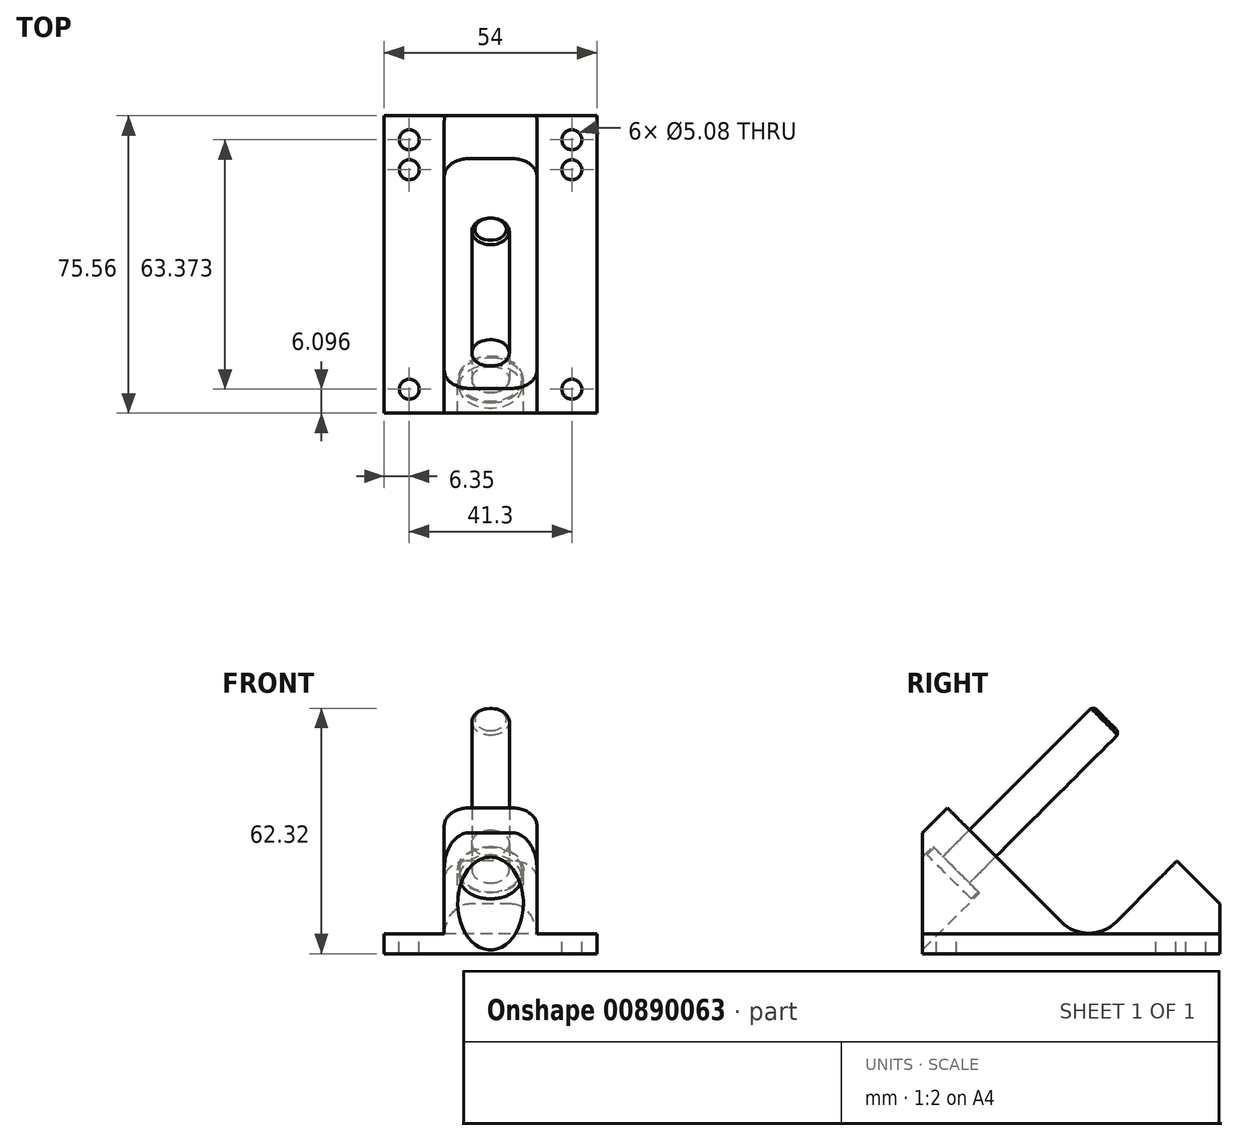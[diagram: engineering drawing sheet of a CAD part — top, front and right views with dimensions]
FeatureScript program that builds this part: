
annotation { "Feature Type Name" : "Feature", "Feature Type Description" : "" }
export const myFeature = defineFeature(function(context is Context, id is Id, definition is map)
    precondition{}
    {
        {
            var Q0;
            Q0=qCreatedBy(makeId("Right.planeOp"),FACE);
            var sketch = newSketch(context, id + "F0", { "sketchPlane" : qUnion([Q0])});
            skLineSegment(sketch, "E0", {"start": v(0, 0) * mm, "end": v(0, 30.72) * mm});
            skLineSegment(sketch, "E1", {"start": v(0, 30.72) * mm, "end": v(6.32, 37.04) * mm});
            skLineSegment(sketch, "E2", {"start": v(6.32, 37.04) * mm, "end": v(42.25, 1.12) * mm});
            skLineSegment(sketch, "E3", {"start": v(42.25, 1.12) * mm, "end": v(64.7, 23.57) * mm});
            skLineSegment(sketch, "E4", {"start": v(64.7, 23.57) * mm, "end": v(75.57, 12.7) * mm});
            skLineSegment(sketch, "E5", {"start": v(75.57, 12.7) * mm, "end": v(75.57, 0) * mm});
            skLineSegment(sketch, "E6", {"start": v(75.57, 0) * mm, "end": v(0, 0) * mm});
            skLineSegment(sketch, "E7", {"start": v(15.3, 28.06) * mm, "end": v(28.77, 41.53) * mm, "construction": true});
            skLineSegment(sketch, "E8", {"start": v(28.77, 41.53) * mm, "end": v(55.72, 14.59) * mm, "construction": true});
            skLineSegment(sketch, "E9", {"start": v(55.72, 14.59) * mm, "end": v(64.7, 5.6) * mm, "construction": true});
            skLineSegment(sketch, "E10", {"start": v(64.7, 5.6) * mm, "end": v(70.08, 11) * mm, "construction": true});
            skLineSegment(sketch, "E11", {"start": v(70.08, 11) * mm, "end": v(61.1, 19.98) * mm, "construction": true});
            skLineSegment(sketch, "E12", {"start": v(28.77, 41.53) * mm, "end": v(15.3, 55) * mm, "construction": true});
            skCircle(sketch, "E13", {"center": v(15.3, 55) * mm, "radius": 4 * mm, "construction": true});
            skLineSegment(sketch, "E14", {"start": v(64.7, 5.6) * mm, "end": v(59.3, 0.22) * mm, "construction": true});
            skLineSegment(sketch, "E15", {"start": v(59.3, 0.22) * mm, "end": v(50.33, 9.2) * mm, "construction": true});
            skCircle(sketch, "E16", {"center": v(57.51, 12.8) * mm, "radius": 5.08 * mm, "construction": true});
            skSolve(sketch);
        }
        {
            var Q0;
            Q0 = qSketchRegion(id + "F0", true);
            extrude(context, id + "F1", {"entities" : qUnion([Q0]), "depth" : 27 * mm, "offsetDistance" : 25.4 * mm});
        }
        {
            var Q0;
            Q0=makeQuery(id+"F1.opExtrude","SWEPT_EDGE",EDGE,{"disambiguationData":[OSD([sQuery(id+"F0.wireOp",EDGE,"E2"),sQuery(id+"F0.wireOp",EDGE,"E3")])]});
            fillet(context, id + "F2", {"entities" : qUnion([Q0]), "radius" : 9.9 * mm, "tangentPropagation" : true, "allowEdgeOverflow" : false});
        }
        {
            var Q0;
            Q0=makeQuery(id+"F1.opExtrude","CAP_FACE",FACE,{"disambiguationData":[OSD([sQuery(id+"F0.wireOp",EDGE,"E0"),sQuery(id+"F0.wireOp",EDGE,"E1"),sQuery(id+"F0.wireOp",EDGE,"E2"),sQuery(id+"F0.wireOp",EDGE,"E3"),sQuery(id+"F0.wireOp",EDGE,"E4"),sQuery(id+"F0.wireOp",EDGE,"E5"),sQuery(id+"F0.wireOp",EDGE,"E6")])],"isStart":false});
            var sketch = newSketch(context, id + "F3", { "sketchPlane" : qUnion([Q0])});
            skPoint(sketch, "E17.oppositeSnap0", {"position": v(75.57, 6.35) * mm});
            skLineSegment(sketch, "E17.bottom", {"start": v(0, 5.08) * mm, "end": v(75.57, 5.08) * mm});
            skLineSegment(sketch, "E17.top", {"start": v(0, 37.04) * mm, "end": v(75.57, 37.04) * mm});
            skLineSegment(sketch, "E17.left", {"start": v(0, 5.08) * mm, "end": v(0, 37.04) * mm});
            skLineSegment(sketch, "E17.right", {"start": v(75.57, 5.08) * mm, "end": v(75.57, 37.04) * mm});
            skSolve(sketch);
        }
        {
            var Q0;
            Q0 = qSketchRegion(id + "F3", true);
            extrude(context, id + "F4", {"entities" : qUnion([Q0]), "operationType" : NewBodyOperationType.REMOVE, "oppositeDirection" : true, "depth" : 15.24 * mm, "offsetDistance" : 25.4 * mm});
        }
        {
            var Q0;
            Q0=makeQuery(id+"F4.boolean.opBoolean","COPY",FACE,{"derivedFrom":makeQuery(id+"F4.opExtrude","SWEPT_FACE",FACE,{"disambiguationData":[OSD([sQuery(id+"F3.wireOp",EDGE,"E17.bottom")])]})});
            var sketch = newSketch(context, id + "F5", { "sketchPlane" : qUnion([Q0])});
            skLineSegment(sketch, "E18", {"start": v(20.65, 69.47) * mm, "end": v(20.65, 61.85) * mm, "construction": true});
            skLineSegment(sketch, "E19", {"start": v(20.65, 61.85) * mm, "end": v(20.65, 6.1) * mm, "construction": true});
            skCircle(sketch, "E20", {"center": v(20.65, 69.47) * mm, "radius": 2.54 * mm});
            skCircle(sketch, "E21", {"center": v(20.65, 61.85) * mm, "radius": 2.54 * mm});
            skCircle(sketch, "E22", {"center": v(20.65, 6.1) * mm, "radius": 2.54 * mm});
            skSolve(sketch);
        }
        {
            var Q0;
            Q0 = qSketchRegion(id + "F5", true);
            extrude(context, id + "F6", {"entities" : qUnion([Q0]), "operationType" : NewBodyOperationType.REMOVE, "endBound" : BoundingType.THROUGH_ALL, "oppositeDirection" : true, "depth" : 25.4 * mm, "offsetDistance" : 25.4 * mm});
        }
        {
            var Q0;
            Q0=makeQuery(id+"F1.opExtrude","SWEPT_BODY",BODY,{"disambiguationData":[OSD([sQuery(id+"F0.wireOp",EDGE,"E0"),sQuery(id+"F0.wireOp",EDGE,"E1"),sQuery(id+"F0.wireOp",EDGE,"E2"),sQuery(id+"F0.wireOp",EDGE,"E3"),sQuery(id+"F0.wireOp",EDGE,"E4"),sQuery(id+"F0.wireOp",EDGE,"E5"),sQuery(id+"F0.wireOp",EDGE,"E6")])]});
            var Q1;
            Q1=makeQuery(id+"F1.opExtrude","CAP_FACE",FACE,{"disambiguationData":[OSD([sQuery(id+"F0.wireOp",EDGE,"E0"),sQuery(id+"F0.wireOp",EDGE,"E1"),sQuery(id+"F0.wireOp",EDGE,"E2"),sQuery(id+"F0.wireOp",EDGE,"E3"),sQuery(id+"F0.wireOp",EDGE,"E4"),sQuery(id+"F0.wireOp",EDGE,"E5"),sQuery(id+"F0.wireOp",EDGE,"E6")])],"isStart":true});
            mirror(context, id + "F7", {"operationType" : NewBodyOperationType.ADD, "entities" : qUnion([Q0]), "mirrorPlane" : qUnion([Q1])});
        }
        {
            var Q0;
            Q0=makeQuery(id+"F7.opPattern","COPY",EDGE,{"derivedFrom":makeQuery(id+"F4.boolean.opBoolean","INTERSECT",EDGE,{"derivedFrom":[makeQuery(id+"F1.opExtrude","SWEPT_FACE",FACE,{"disambiguationData":[OSD([sQuery(id+"F0.wireOp",EDGE,"E1")])]}),makeQuery(id+"F4.opExtrude","CAP_FACE",FACE,{"disambiguationData":[OSD([sQuery(id+"F3.wireOp",EDGE,"E17.bottom"),sQuery(id+"F3.wireOp",EDGE,"E17.top"),sQuery(id+"F3.wireOp",EDGE,"E17.left"),sQuery(id+"F3.wireOp",EDGE,"E17.right")])],"isStart":false})]}),"instanceName":"1"});
            var Q1;
            Q1=makeQuery(id+"F4.boolean.opBoolean","INTERSECT",EDGE,{"derivedFrom":[makeQuery(id+"F1.opExtrude","SWEPT_FACE",FACE,{"disambiguationData":[OSD([sQuery(id+"F0.wireOp",EDGE,"E1")])]}),makeQuery(id+"F4.opExtrude","CAP_FACE",FACE,{"disambiguationData":[OSD([sQuery(id+"F3.wireOp",EDGE,"E17.bottom"),sQuery(id+"F3.wireOp",EDGE,"E17.top"),sQuery(id+"F3.wireOp",EDGE,"E17.left"),sQuery(id+"F3.wireOp",EDGE,"E17.right")])],"isStart":false})]});
            var Q2;
            Q2=makeQuery(id+"F7.opPattern","COPY",EDGE,{"derivedFrom":makeQuery(id+"F4.boolean.opBoolean","INTERSECT",EDGE,{"derivedFrom":[makeQuery(id+"F1.opExtrude","SWEPT_FACE",FACE,{"disambiguationData":[OSD([sQuery(id+"F0.wireOp",EDGE,"E4")])]}),makeQuery(id+"F4.opExtrude","CAP_FACE",FACE,{"disambiguationData":[OSD([sQuery(id+"F3.wireOp",EDGE,"E17.bottom"),sQuery(id+"F3.wireOp",EDGE,"E17.top"),sQuery(id+"F3.wireOp",EDGE,"E17.left"),sQuery(id+"F3.wireOp",EDGE,"E17.right")])],"isStart":false})]}),"instanceName":"1"});
            var Q3;
            Q3=makeQuery(id+"F4.boolean.opBoolean","INTERSECT",EDGE,{"derivedFrom":[makeQuery(id+"F1.opExtrude","SWEPT_FACE",FACE,{"disambiguationData":[OSD([sQuery(id+"F0.wireOp",EDGE,"E4")])]}),makeQuery(id+"F4.opExtrude","CAP_FACE",FACE,{"disambiguationData":[OSD([sQuery(id+"F3.wireOp",EDGE,"E17.bottom"),sQuery(id+"F3.wireOp",EDGE,"E17.top"),sQuery(id+"F3.wireOp",EDGE,"E17.left"),sQuery(id+"F3.wireOp",EDGE,"E17.right")])],"isStart":false})]});
            fillet(context, id + "F8", {"entities" : qUnion([Q0, Q1, Q2, Q3]), "radius" : 6.35 * mm, "tangentPropagation" : true, "allowEdgeOverflow" : false});
        }
        {
            var Q0;
            Q0=qCreatedBy(makeId("Right.planeOp"),FACE);
            var sketch = newSketch(context, id + "F9", { "sketchPlane" : qUnion([Q0])});
            skLineSegment(sketch, "E23.0", {"start": v(6.32, 37.04) * mm, "end": v(42.25, 1.12) * mm});
            skLineSegment(sketch, "E23.1", {"start": v(15.3, 28.06) * mm, "end": v(28.77, 41.53) * mm, "construction": true});
            skLineSegment(sketch, "E24", {"start": v(11.94, 31.43) * mm, "end": v(5.2, 24.7) * mm});
            skLineSegment(sketch, "E25", {"start": v(5.2, 24.7) * mm, "end": v(2.67, 27.22) * mm});
            skLineSegment(sketch, "E26", {"start": v(2.67, 27.22) * mm, "end": v(-12.28, 12.28) * mm});
            skLineSegment(sketch, "E27", {"start": v(-12.28, 12.28) * mm, "end": v(-6.38, 6.38) * mm});
            skLineSegment(sketch, "E28", {"start": v(-6.38, 6.38) * mm, "end": v(15.3, 28.06) * mm});
            skLineSegment(sketch, "E29", {"start": v(-6.38, 6.38) * mm, "end": v(0, 0) * mm, "construction": true});
            skSolve(sketch);
        }
        {
            var Q0;
            Q0 = qSketchRegion(id + "F9", true);
            var Q1;
            Q1=sQuery(id+"F9.wireOp",EDGE,"E23.1");
            revolve(context, id + "F10", {"operationType" : NewBodyOperationType.REMOVE, "surfaceOperationType" : NewSurfaceOperationType.NEW, "entities" : qUnion([Q0]), "axis" : qUnion([Q1]), "revolveType" : RevolveType.FULL, "oppositeDirection" : true});
        }
        {
            var Q0;
            Q0=qCreatedBy(makeId("Right.planeOp"),FACE);
            var sketch = newSketch(context, id + "F11", { "sketchPlane" : qUnion([Q0])});
            skLineSegment(sketch, "E30.1", {"start": v(5.2, 24.7) * mm, "end": v(2.96, 26.94) * mm});
            skLineSegment(sketch, "E30.2", {"start": v(11.94, 31.43) * mm, "end": v(5.2, 24.7) * mm});
            skLineSegment(sketch, "E31", {"start": v(2.96, 26.94) * mm, "end": v(1.16, 25.14) * mm});
            skPoint(sketch, "E30.0.end.orphan", {"position": v(-12.28, 12.28) * mm});
            skPoint(sketch, "E30.0.start.orphan", {"position": v(2.67, 27.22) * mm});
            skLineSegment(sketch, "E32", {"start": v(1.16, 25.14) * mm, "end": v(6.77, 19.53) * mm});
            skLineSegment(sketch, "E33", {"start": v(6.77, 19.53) * mm, "end": v(46.74, 59.5) * mm});
            skLineSegment(sketch, "E34", {"start": v(46.74, 59.5) * mm, "end": v(43.37, 62.86) * mm});
            skLineSegment(sketch, "E35", {"start": v(43.37, 62.86) * mm, "end": v(11.94, 31.43) * mm});
            skSolve(sketch);
        }
        {
            var Q0;
            Q0 = qSketchRegion(id + "F11", true);
            var Q1;
            Q1=sQuery(id+"F11.wireOp",EDGE,"E33");
            revolve(context, id + "F12", {"surfaceOperationType" : NewSurfaceOperationType.NEW, "entities" : qUnion([Q0]), "axis" : qUnion([Q1]), "revolveType" : RevolveType.FULL});
        }
        {
            var Q0;
            Q0=makeQuery(id+"F12.opRevolve","SWEPT_EDGE",EDGE,{"disambiguationData":[OSD([sQuery(id+"F11.wireOp",EDGE,"E34"),sQuery(id+"F11.wireOp",EDGE,"E35")])]});
            chamfer(context, id + "F13", {"entities" : qUnion([Q0]), "width" : 0.76 * mm, "tangentPropagation" : true});
        }
    });
